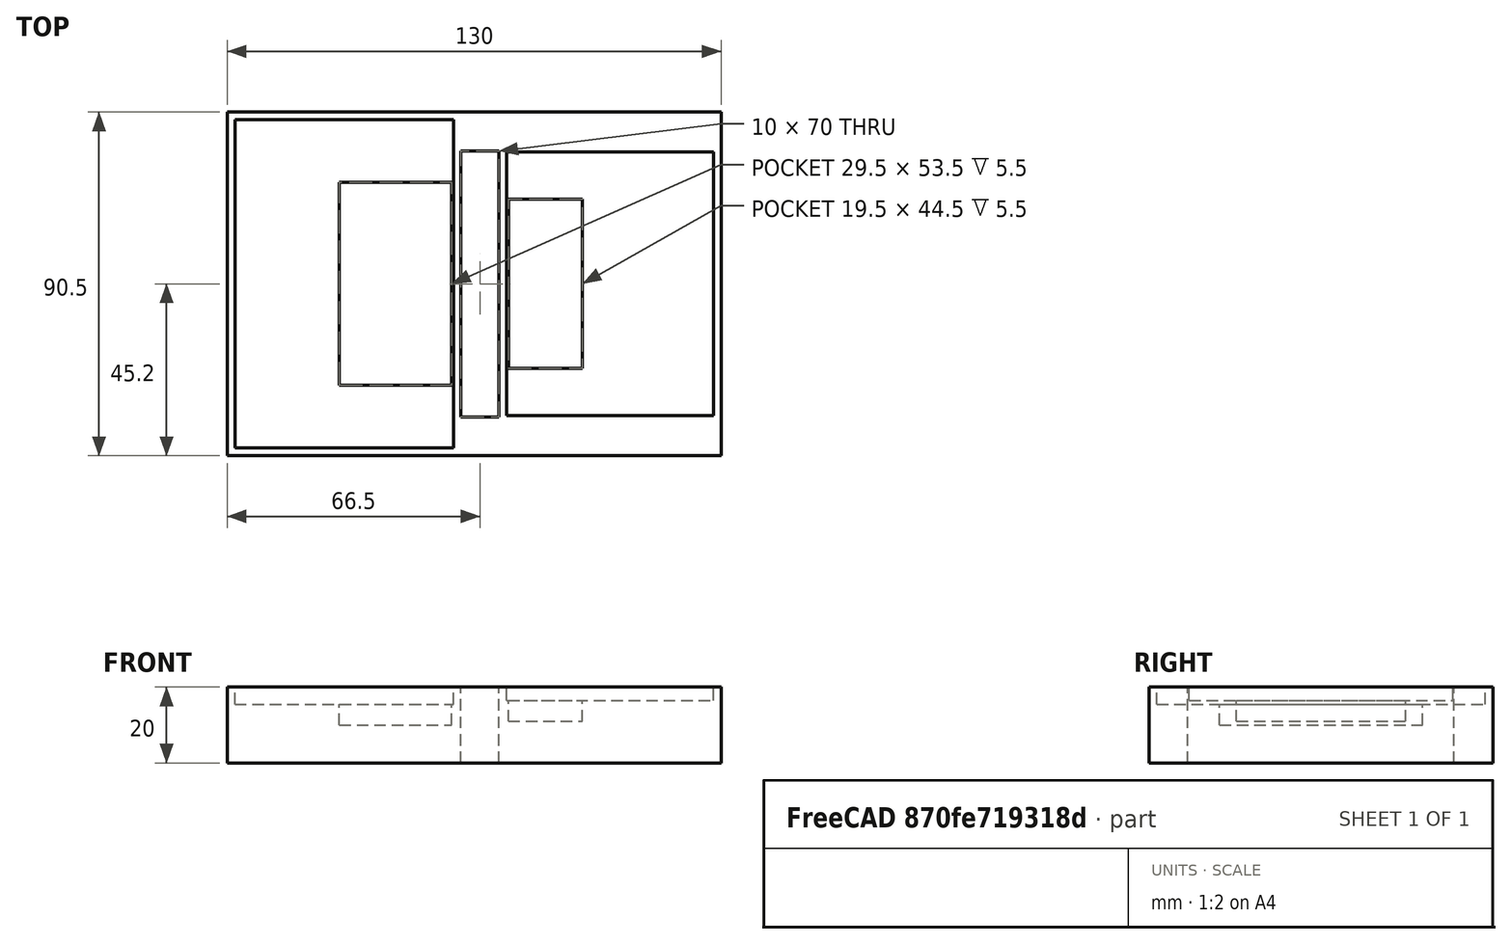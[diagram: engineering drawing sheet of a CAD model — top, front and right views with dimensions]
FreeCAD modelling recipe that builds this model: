
FCSTD DOCUMENT  (FreeCAD 0.18R16131 (Git))
Label: Seats
License: All rights reserved
LicenseURL: http://en.wikipedia.org/wiki/All_rights_reserved
objects: Part::Box×6, Part::FeaturePython×1
note: 7 computed .brp shape members not serialized (recipe doc carries the construction recipe); baked Part::Feature solids carry a one-line shape summary decoded from their .brp

FEATURE [Part::Box] Box  label="Cubo"
  AttacherType = Attacher::AttachEngine3D
  Height = 20
  Length = 130
  Width = 90.5
FEATURE [Part::Box] Box001  label="RASP"
  AttacherType = Attacher::AttachEngine3D
  Height = 4.5
  Length = 57.5
  Placement = pos=(2,2,15.5) rot=(0,0,1;0rad)
  Width = 86.5
FEATURE [Part::Box] Box002  label="ESP"
  AttacherType = Attacher::AttachEngine3D
  Height = 5.5
  Length = 29.5
  Placement = pos=(29.5,18.5,10) rot=(0,0,1;0rad)
  Width = 53.5
FEATURE [Part::Box] Box003  label="Arduino_nano"
  AttacherType = Attacher::AttachEngine3D
  Height = 5.5
  Length = 19.5
  Placement = pos=(74,23,11) rot=(0,0,1;0rad)
  Width = 44.5
FEATURE [Part::Box] Box004  label="buraco"
  AttacherType = Attacher::AttachEngine3D
  Height = 20
  Length = 10
  Placement = pos=(61.5,10.2,0) rot=(0,0,1;0rad)
  Width = 70
FEATURE [Part::Box] Box005  label="Arduino"
  AttacherType = Attacher::AttachEngine3D
  Height = 3.5
  Length = 54.5
  Placement = pos=(73.5,10.5,16.5) rot=(0,0,1;0rad)
  Width = 69.5
FEATURE [Part::FeaturePython] XOR  # WARN: FeaturePython — macro-defined, semantics opaque (R4)
  Objects = -> [Box,Box004,Box005,Box002,Box001,Box003]
  Tolerance = 0
